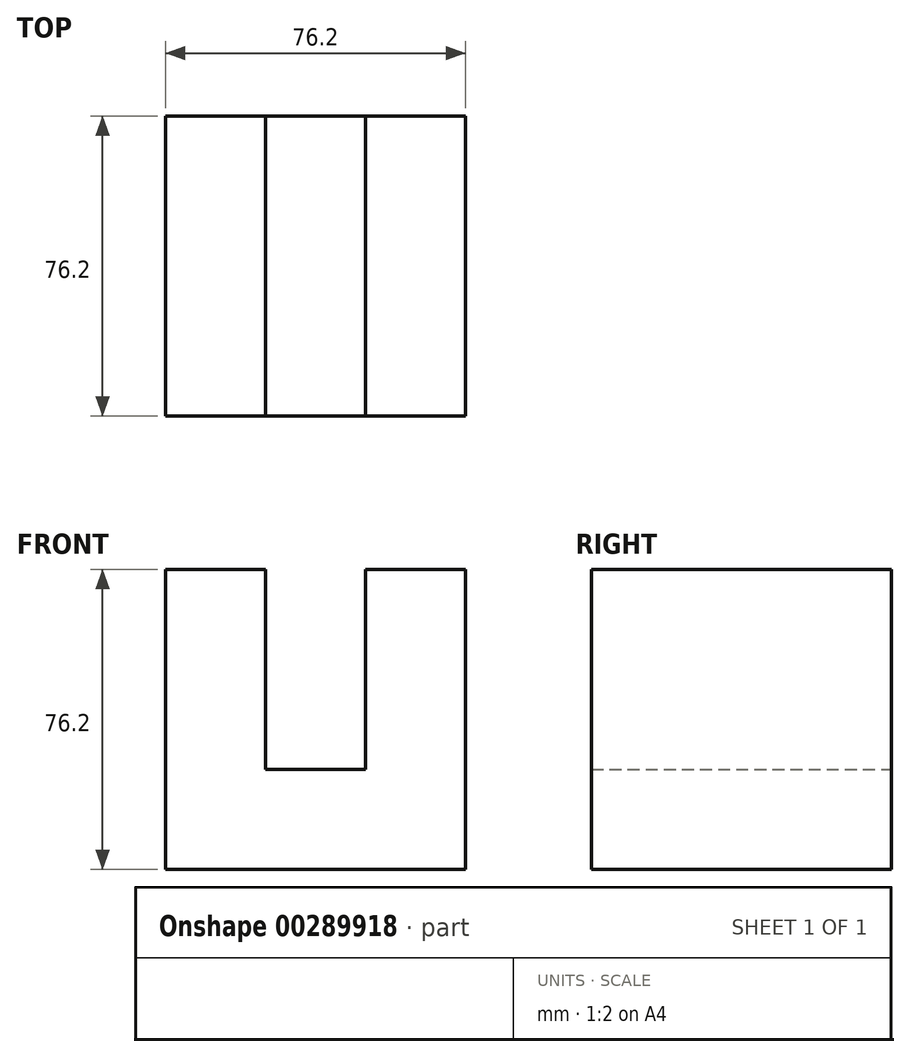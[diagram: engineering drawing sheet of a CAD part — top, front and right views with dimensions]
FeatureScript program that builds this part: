
annotation { "Feature Type Name" : "Feature", "Feature Type Description" : "" }
export const myFeature = defineFeature(function(context is Context, id is Id, definition is map)
    precondition{}
    {
        {
            var Q0;
            Q0=qCreatedBy(makeId("Front.planeOp"),FACE);
            var sketch = newSketch(context, id + "F0", { "sketchPlane" : qUnion([Q0])});
            skLineSegment(sketch, "E0", {"start": v(0, 0) * mm, "end": v(-76.2, 0) * mm});
            skLineSegment(sketch, "E1", {"start": v(-76.2, 0) * mm, "end": v(-76.2, 76.2) * mm});
            skLineSegment(sketch, "E2", {"start": v(-76.2, 76.2) * mm, "end": v(-50.8, 76.2) * mm});
            skLineSegment(sketch, "E3", {"start": v(-50.8, 76.2) * mm, "end": v(-50.8, 25.4) * mm});
            skLineSegment(sketch, "E4", {"start": v(-25.4, 25.4) * mm, "end": v(-50.8, 25.4) * mm});
            skLineSegment(sketch, "E5", {"start": v(-25.4, 25.4) * mm, "end": v(-25.4, 76.2) * mm});
            skLineSegment(sketch, "E6", {"start": v(-25.4, 76.2) * mm, "end": v(0, 76.2) * mm});
            skLineSegment(sketch, "E7", {"start": v(0, 76.2) * mm, "end": v(0, 0) * mm});
            skSolve(sketch);
        }
        {
            var Q0;
            Q0=makeQuery(id+"F0.imprint","IMPRINT",FACE,{"disambiguationData":[TD([[makeQuery(id+"F0.imprint","IMPRINT",EDGE,{"derivedFrom":sQuery(id+"F0.wireOp",EDGE,"E0")}),-1.0]])]});
            extrude(context, id + "F1", {"entities" : qUnion([Q0]), "depth" : 76.2 * mm});
        }
    });
